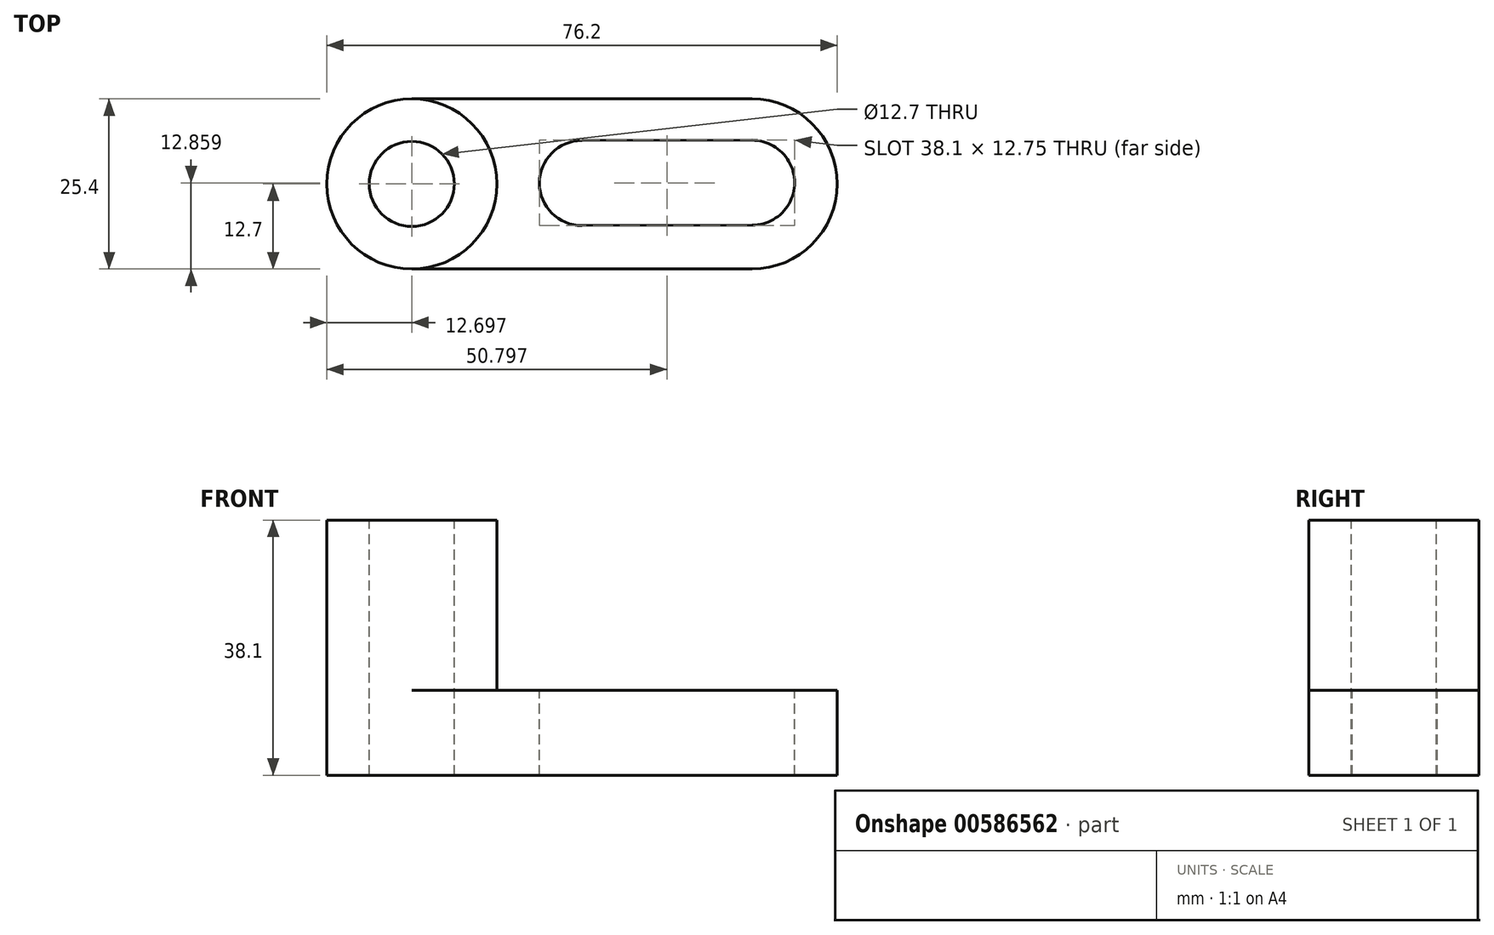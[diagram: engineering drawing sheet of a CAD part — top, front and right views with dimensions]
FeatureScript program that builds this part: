
annotation { "Feature Type Name" : "Feature", "Feature Type Description" : "" }
export const myFeature = defineFeature(function(context is Context, id is Id, definition is map)
    precondition{}
    {
        {
            var Q0;
            Q0=qCreatedBy(makeId("Front.planeOp"),FACE);
            var sketch = newSketch(context, id + "F0", { "sketchPlane" : qUnion([Q0])});
            skLineSegment(sketch, "E0", {"start": v(-71.16, 47.3) * mm, "end": v(-71.16, 9.2) * mm});
            skLineSegment(sketch, "E1", {"start": v(-71.16, 9.2) * mm, "end": v(5.04, 9.2) * mm});
            skLineSegment(sketch, "E2", {"start": v(5.04, 9.2) * mm, "end": v(5.04, 21.9) * mm});
            skLineSegment(sketch, "E3", {"start": v(5.04, 21.9) * mm, "end": v(-45.76, 21.9) * mm});
            skLineSegment(sketch, "E4", {"start": v(-45.76, 21.9) * mm, "end": v(-45.76, 47.3) * mm});
            skLineSegment(sketch, "E5", {"start": v(-45.76, 47.3) * mm, "end": v(-71.16, 47.3) * mm});
            skSolve(sketch);
        }
        {
            var Q0;
            Q0 = qSketchRegion(id + "F0", true);
            extrude(context, id + "F1", {"entities" : qUnion([Q0]), "depth" : 25.4 * mm, "offsetDistance" : 25.4 * mm});
        }
        {
            var Q0;
            Q0=makeQuery(id+"F1.opExtrude","SWEPT_FACE",FACE,{"disambiguationData":[OSD([sQuery(id+"F0.wireOp",EDGE,"E5")])]});
            var sketch = newSketch(context, id + "F2", { "sketchPlane" : qUnion([Q0])});
            skArc(sketch, "E6", {"start": v(-58.46, 0) * mm, "mid": v(-71.16, -12.7) * mm, "end": v(-58.46, -25.4) * mm});
            skSolve(sketch);
        }
        {
            var Q0;
            Q0 = qSketchRegion(id + "F2", true);
            var Q1;
            {var subQ0=sQuery(id+"F2.wireOp",EDGE,"E6");var subQ1=sQuery(id+"F0.wireOp",EDGE,"E5");var subQ2=makeQuery(id+"F1.opExtrude","CAP_EDGE",EDGE,{"disambiguationData":[OSD([subQ1])],"isStart":true});var subQ3=makeQuery(id+"F2.imprint","INTERSECT",VERTEX,{"derivedFrom":[subQ2,subQ0]});Q1=makeQuery(id+"F2.imprint","IMPRINT",FACE,{"disambiguationData":[TD([[makeQuery(id+"F2.imprint","IMPRINT",EDGE,{"disambiguationData":[TD([[subQ3,-1.0]])],"derivedFrom":subQ0}),-1.0]])]});}
            var Q2;
            {var subQ0=sQuery(id+"F2.wireOp",EDGE,"E6");var subQ1=sQuery(id+"F0.wireOp",EDGE,"E5");var subQ2=makeQuery(id+"F1.opExtrude","CAP_EDGE",EDGE,{"disambiguationData":[OSD([subQ1])],"isStart":false});var subQ3=makeQuery(id+"F2.imprint","INTERSECT",VERTEX,{"derivedFrom":[subQ2,subQ0]});Q2=makeQuery(id+"F2.imprint","IMPRINT",FACE,{"disambiguationData":[TD([[makeQuery(id+"F2.imprint","IMPRINT",EDGE,{"disambiguationData":[TD([[subQ3,1.0]])],"derivedFrom":subQ0}),-1.0]])]});}
            extrude(context, id + "F3", {"entities" : qUnion([Q0, Q1, Q2]), "operationType" : NewBodyOperationType.REMOVE, "oppositeDirection" : true, "depth" : 38.1 * mm, "offsetDistance" : 25.4 * mm});
        }
        {
            var Q0;
            Q0=makeQuery(id+"F1.opExtrude","SWEPT_FACE",FACE,{"disambiguationData":[OSD([sQuery(id+"F0.wireOp",EDGE,"E5")])]});
            var sketch = newSketch(context, id + "F4", { "sketchPlane" : qUnion([Q0])});
            skArc(sketch, "E7", {"start": v(-58.46, -25.4) * mm, "mid": v(-45.76, -12.7) * mm, "end": v(-58.46, 0) * mm});
            skSolve(sketch);
        }
        {
            var Q0;
            Q0 = qSketchRegion(id + "F4", true);
            var Q1;
            {var subQ1=sQuery(id+"F0.wireOp",EDGE,"E5");var subQ2=makeQuery(id+"F1.opExtrude","CAP_EDGE",EDGE,{"disambiguationData":[OSD([subQ1])],"isStart":true});var subQ3=subQ2;Q1=makeQuery(id+"F4.imprint","IMPRINT",FACE,{"disambiguationData":[TD([[makeQuery(id+"F4.imprint","IMPRINT",EDGE,{"derivedFrom":subQ3}),1.0]])]});}
            var Q2;
            {var subQ1=sQuery(id+"F0.wireOp",EDGE,"E5");var subQ2=makeQuery(id+"F1.opExtrude","CAP_EDGE",EDGE,{"disambiguationData":[OSD([subQ1])],"isStart":false});var subQ3=subQ2;Q2=makeQuery(id+"F4.imprint","IMPRINT",FACE,{"disambiguationData":[TD([[makeQuery(id+"F4.imprint","IMPRINT",EDGE,{"derivedFrom":subQ3}),-1.0]])]});}
            extrude(context, id + "F5", {"entities" : qUnion([Q0, Q1, Q2]), "operationType" : NewBodyOperationType.REMOVE, "oppositeDirection" : true, "depth" : 25.4 * mm, "offsetDistance" : 25.4 * mm});
        }
        {
            var Q0;
            {var subQ0=sQuery(id+"F0.wireOp",EDGE,"E5");var subQ1=makeQuery(id+"F1.opExtrude","CAP_EDGE",EDGE,{"disambiguationData":[OSD([subQ0])],"isStart":true});var subQ2=subQ1;var subQ3=sQuery(id+"F0.wireOp",EDGE,"E4");var subQ4=makeQuery(id+"F1.opExtrude","SWEPT_EDGE",EDGE,{"disambiguationData":[OSD([subQ3,subQ0])]});var subQ5=sQuery(id+"F4.wireOp",EDGE,"E7");var subQ6=makeQuery(id+"F4.imprint","INTERSECT",VERTEX,{"derivedFrom":[subQ4,subQ5]});var subQ8=makeQuery(id+"F1.opExtrude","CAP_EDGE",EDGE,{"disambiguationData":[OSD([subQ0])],"isStart":false});var subQ11=subQ8;Q0=makeQuery(id+"F5.boolean.opBoolean","MERGE",FACE,{"derivedFrom":[makeQuery(id+"F1.opExtrude","SWEPT_FACE",FACE,{"disambiguationData":[OSD([sQuery(id+"F0.wireOp",EDGE,"E3")])]}),makeQuery(id+"F5.opExtrude","CAP_FACE",FACE,{"disambiguationData":[OSD([subQ3,subQ0,subQ5]),TDD([makeQuery(id+"F4.imprint","IMPRINT",EDGE,{"disambiguationData":[TD([[subQ6,1.0]])],"derivedFrom":subQ5}),makeQuery(id+"F4.imprint","IMPRINT",EDGE,{"derivedFrom":subQ11}),makeQuery(id+"F4.imprint","IMPRINT",EDGE,{"disambiguationData":[TD([[makeQuery(id+"F4.imprint","INTERSECT",VERTEX,{"derivedFrom":[subQ4,subQ11]}),-1.0]])],"derivedFrom":subQ4})])],"isStart":false}),makeQuery(id+"F5.opExtrude","CAP_FACE",FACE,{"disambiguationData":[OSD([subQ3,subQ0,subQ5]),TDD([makeQuery(id+"F4.imprint","IMPRINT",EDGE,{"disambiguationData":[TD([[subQ6,-1.0]])],"derivedFrom":subQ5}),makeQuery(id+"F4.imprint","IMPRINT",EDGE,{"derivedFrom":subQ2}),makeQuery(id+"F4.imprint","IMPRINT",EDGE,{"disambiguationData":[TD([[makeQuery(id+"F4.imprint","INTERSECT",VERTEX,{"derivedFrom":[subQ4,subQ2]}),1.0]])],"derivedFrom":subQ4})])],"isStart":false})]});}
            var sketch = newSketch(context, id + "F6", { "sketchPlane" : qUnion([Q0])});
            skArc(sketch, "E8", {"start": v(-7.66, -25.4) * mm, "mid": v(5.04, -12.7) * mm, "end": v(-7.66, 0) * mm});
            skSolve(sketch);
        }
        {
            var Q0;
            Q0 = qSketchRegion(id + "F6", true);
            var Q1;
            {var subQ0=sQuery(id+"F6.wireOp",EDGE,"E8");var subQ2=sQuery(id+"F0.wireOp",EDGE,"E3");var subQ5=makeQuery(id+"F1.opExtrude","SWEPT_EDGE",EDGE,{"disambiguationData":[OSD([sQuery(id+"F0.wireOp",EDGE,"E2"),subQ2])]});var subQ6=makeQuery(id+"F6.imprint","INTERSECT",VERTEX,{"derivedFrom":[subQ5,subQ0]});Q1=makeQuery(id+"F6.imprint","IMPRINT",FACE,{"disambiguationData":[TD([[makeQuery(id+"F6.imprint","IMPRINT",EDGE,{"disambiguationData":[TD([[subQ6,-1.0]])],"derivedFrom":subQ0}),-1.0]])]});}
            var Q2;
            {var subQ0=sQuery(id+"F6.wireOp",EDGE,"E8");var subQ2=sQuery(id+"F0.wireOp",EDGE,"E3");var subQ5=makeQuery(id+"F1.opExtrude","SWEPT_EDGE",EDGE,{"disambiguationData":[OSD([sQuery(id+"F0.wireOp",EDGE,"E2"),subQ2])]});var subQ6=makeQuery(id+"F6.imprint","INTERSECT",VERTEX,{"derivedFrom":[subQ5,subQ0]});Q2=makeQuery(id+"F6.imprint","IMPRINT",FACE,{"disambiguationData":[TD([[makeQuery(id+"F6.imprint","IMPRINT",EDGE,{"disambiguationData":[TD([[subQ6,1.0]])],"derivedFrom":subQ0}),-1.0]])]});}
            extrude(context, id + "F7", {"entities" : qUnion([Q0, Q1, Q2]), "operationType" : NewBodyOperationType.REMOVE, "oppositeDirection" : true, "depth" : 25.4 * mm, "offsetDistance" : 25.4 * mm});
        }
        {
            var Q0;
            {var subQ0=sQuery(id+"F0.wireOp",EDGE,"E5");var subQ1=makeQuery(id+"F1.opExtrude","CAP_EDGE",EDGE,{"disambiguationData":[OSD([subQ0])],"isStart":true});var subQ2=subQ1;var subQ3=sQuery(id+"F0.wireOp",EDGE,"E4");var subQ4=makeQuery(id+"F1.opExtrude","SWEPT_EDGE",EDGE,{"disambiguationData":[OSD([subQ3,subQ0])]});var subQ5=sQuery(id+"F4.wireOp",EDGE,"E7");var subQ6=makeQuery(id+"F4.imprint","INTERSECT",VERTEX,{"derivedFrom":[subQ4,subQ5]});var subQ8=makeQuery(id+"F1.opExtrude","CAP_EDGE",EDGE,{"disambiguationData":[OSD([subQ0])],"isStart":false});var subQ11=subQ8;Q0=makeQuery(id+"F5.boolean.opBoolean","MERGE",FACE,{"derivedFrom":[makeQuery(id+"F1.opExtrude","SWEPT_FACE",FACE,{"disambiguationData":[OSD([sQuery(id+"F0.wireOp",EDGE,"E3")])]}),makeQuery(id+"F5.opExtrude","CAP_FACE",FACE,{"disambiguationData":[OSD([subQ3,subQ0,subQ5]),TDD([makeQuery(id+"F4.imprint","IMPRINT",EDGE,{"disambiguationData":[TD([[subQ6,1.0]])],"derivedFrom":subQ5}),makeQuery(id+"F4.imprint","IMPRINT",EDGE,{"derivedFrom":subQ11}),makeQuery(id+"F4.imprint","IMPRINT",EDGE,{"disambiguationData":[TD([[makeQuery(id+"F4.imprint","INTERSECT",VERTEX,{"derivedFrom":[subQ4,subQ11]}),-1.0]])],"derivedFrom":subQ4})])],"isStart":false}),makeQuery(id+"F5.opExtrude","CAP_FACE",FACE,{"disambiguationData":[OSD([subQ3,subQ0,subQ5]),TDD([makeQuery(id+"F4.imprint","IMPRINT",EDGE,{"disambiguationData":[TD([[subQ6,-1.0]])],"derivedFrom":subQ5}),makeQuery(id+"F4.imprint","IMPRINT",EDGE,{"derivedFrom":subQ2}),makeQuery(id+"F4.imprint","IMPRINT",EDGE,{"disambiguationData":[TD([[makeQuery(id+"F4.imprint","INTERSECT",VERTEX,{"derivedFrom":[subQ4,subQ2]}),1.0]])],"derivedFrom":subQ4})])],"isStart":false})]});}
            var sketch = newSketch(context, id + "F8", { "sketchPlane" : qUnion([Q0])});
            skCircle(sketch, "E9", {"center": v(-7.66, -12.52) * mm, "radius": 6.35 * mm});
            skCircle(sketch, "E10", {"center": v(-33.06, -12.56) * mm, "radius": 6.35 * mm});
            skSolve(sketch);
        }
        {
            var Q0;
            Q0 = qSketchRegion(id + "F8", true);
            extrude(context, id + "F9", {"entities" : qUnion([Q0]), "operationType" : NewBodyOperationType.REMOVE, "oppositeDirection" : true, "depth" : 25.4 * mm, "offsetDistance" : 25.4 * mm});
        }
        {
            var Q0;
            {var subQ0=sQuery(id+"F0.wireOp",EDGE,"E5");var subQ1=makeQuery(id+"F1.opExtrude","CAP_EDGE",EDGE,{"disambiguationData":[OSD([subQ0])],"isStart":true});var subQ2=subQ1;var subQ3=sQuery(id+"F0.wireOp",EDGE,"E4");var subQ4=makeQuery(id+"F1.opExtrude","SWEPT_EDGE",EDGE,{"disambiguationData":[OSD([subQ3,subQ0])]});var subQ5=sQuery(id+"F4.wireOp",EDGE,"E7");var subQ6=makeQuery(id+"F4.imprint","INTERSECT",VERTEX,{"derivedFrom":[subQ4,subQ5]});var subQ8=makeQuery(id+"F1.opExtrude","CAP_EDGE",EDGE,{"disambiguationData":[OSD([subQ0])],"isStart":false});var subQ11=subQ8;Q0=makeQuery(id+"F5.boolean.opBoolean","MERGE",FACE,{"derivedFrom":[makeQuery(id+"F1.opExtrude","SWEPT_FACE",FACE,{"disambiguationData":[OSD([sQuery(id+"F0.wireOp",EDGE,"E3")])]}),makeQuery(id+"F5.opExtrude","CAP_FACE",FACE,{"disambiguationData":[OSD([subQ3,subQ0,subQ5]),TDD([makeQuery(id+"F4.imprint","IMPRINT",EDGE,{"disambiguationData":[TD([[subQ6,1.0]])],"derivedFrom":subQ5}),makeQuery(id+"F4.imprint","IMPRINT",EDGE,{"derivedFrom":subQ11}),makeQuery(id+"F4.imprint","IMPRINT",EDGE,{"disambiguationData":[TD([[makeQuery(id+"F4.imprint","INTERSECT",VERTEX,{"derivedFrom":[subQ4,subQ11]}),-1.0]])],"derivedFrom":subQ4})])],"isStart":false}),makeQuery(id+"F5.opExtrude","CAP_FACE",FACE,{"disambiguationData":[OSD([subQ3,subQ0,subQ5]),TDD([makeQuery(id+"F4.imprint","IMPRINT",EDGE,{"disambiguationData":[TD([[subQ6,-1.0]])],"derivedFrom":subQ5}),makeQuery(id+"F4.imprint","IMPRINT",EDGE,{"derivedFrom":subQ2}),makeQuery(id+"F4.imprint","IMPRINT",EDGE,{"disambiguationData":[TD([[makeQuery(id+"F4.imprint","INTERSECT",VERTEX,{"derivedFrom":[subQ4,subQ2]}),1.0]])],"derivedFrom":subQ4})])],"isStart":false})]});}
            var sketch = newSketch(context, id + "F10", { "sketchPlane" : qUnion([Q0])});
            skLineSegment(sketch, "E11", {"start": v(-33.08, -6.21) * mm, "end": v(-7.68, -6.17) * mm});
            skLineSegment(sketch, "E12", {"start": v(-33.05, -18.91) * mm, "end": v(-7.65, -18.87) * mm});
            skSolve(sketch);
        }
        {
            var Q0;
            Q0 = qSketchRegion(id + "F10", true);
            var Q1;
            {var subQ0=sQuery(id+"F10.wireOp",EDGE,"E11");Q1=makeQuery(id+"F10.imprint","IMPRINT",FACE,{"disambiguationData":[TD([[makeQuery(id+"F10.imprint","IMPRINT",EDGE,{"derivedFrom":subQ0}),-1.0]])]});}
            extrude(context, id + "F11", {"entities" : qUnion([Q0, Q1]), "operationType" : NewBodyOperationType.REMOVE, "oppositeDirection" : true, "depth" : 25.4 * mm, "offsetDistance" : 25.4 * mm});
        }
        {
            var Q0;
            Q0=makeQuery(id+"F1.opExtrude","SWEPT_FACE",FACE,{"disambiguationData":[OSD([sQuery(id+"F0.wireOp",EDGE,"E5")])]});
            var sketch = newSketch(context, id + "F12", { "sketchPlane" : qUnion([Q0])});
            skCircle(sketch, "E13", {"center": v(-58.46, -12.7) * mm, "radius": 6.35 * mm});
            skSolve(sketch);
        }
        {
            var Q0;
            Q0 = qSketchRegion(id + "F12", true);
            extrude(context, id + "F13", {"entities" : qUnion([Q0]), "operationType" : NewBodyOperationType.REMOVE, "endBound" : BoundingType.THROUGH_ALL, "oppositeDirection" : true, "depth" : 25.4 * mm, "offsetDistance" : 25.4 * mm});
        }
    });
